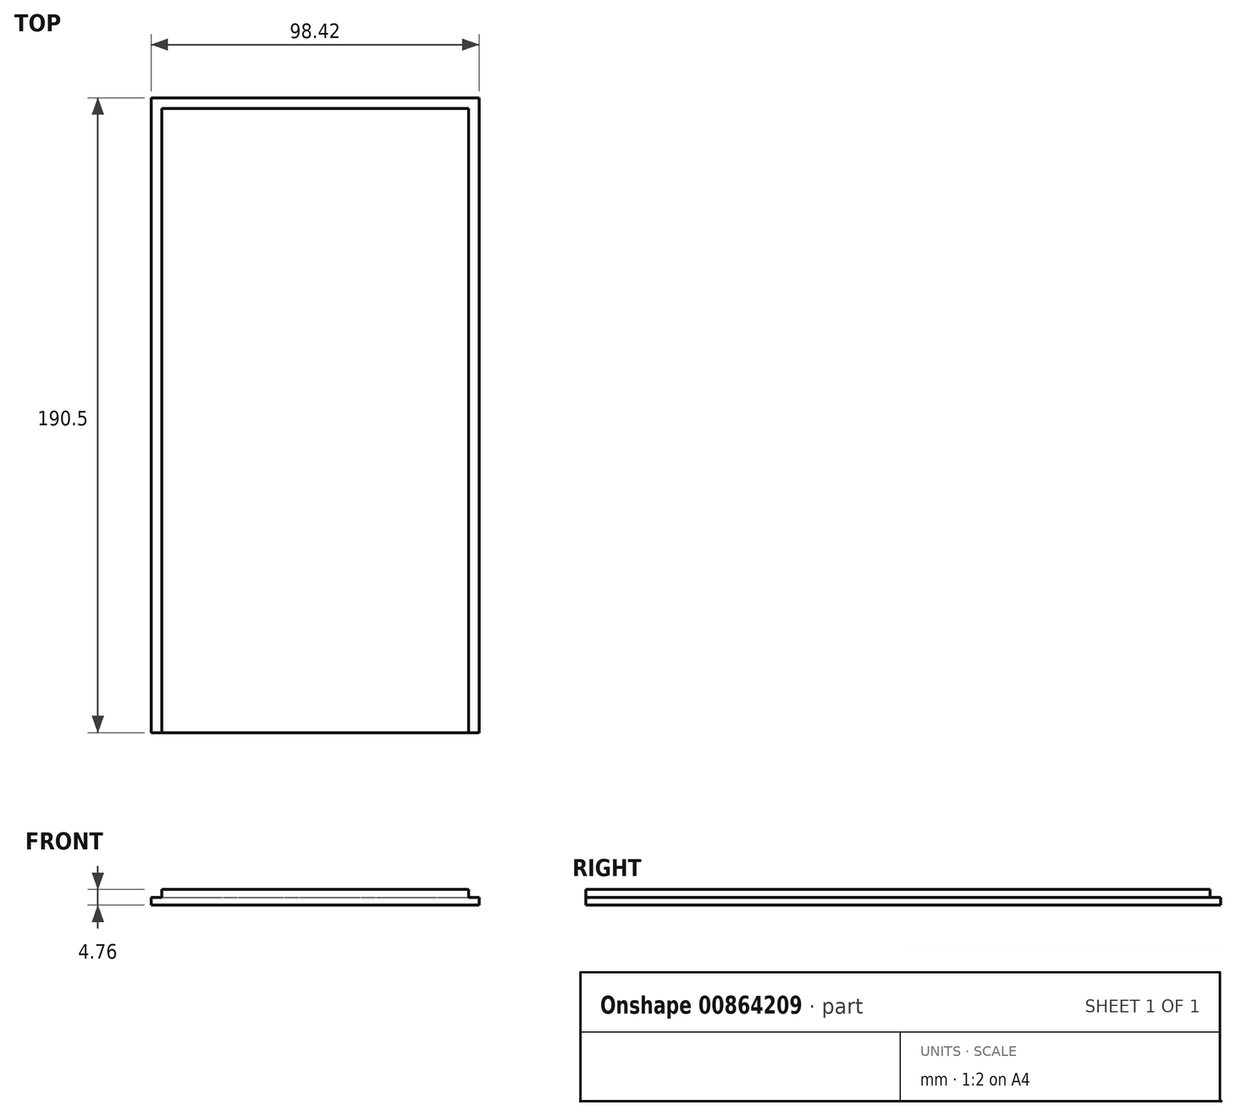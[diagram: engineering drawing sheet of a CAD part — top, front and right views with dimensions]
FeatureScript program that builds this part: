
annotation { "Feature Type Name" : "Feature", "Feature Type Description" : "" }
export const myFeature = defineFeature(function(context is Context, id is Id, definition is map)
    precondition{}
    {
        {
            var Q0;
            Q0=qCreatedBy(makeId("Top.planeOp"),FACE);
            var sketch = newSketch(context, id + "F0", { "sketchPlane" : qUnion([Q0])});
            skLineSegment(sketch, "E0.bottom", {"start": v(-49.21, 95.25) * mm, "end": v(49.21, 95.25) * mm});
            skLineSegment(sketch, "E0.top", {"start": v(-49.21, -95.25) * mm, "end": v(49.21, -95.25) * mm});
            skLineSegment(sketch, "E0.left", {"start": v(-49.21, 95.25) * mm, "end": v(-49.21, -95.25) * mm});
            skLineSegment(sketch, "E0.right", {"start": v(49.21, 95.25) * mm, "end": v(49.21, -95.25) * mm});
            skPoint(sketch, "E0.middle", {"position": v(0, 0) * mm});
            skLineSegment(sketch, "E1", {"start": v(-46.04, -95.25) * mm, "end": v(-46.04, 92.08) * mm});
            skLineSegment(sketch, "E2", {"start": v(-46.04, 92.08) * mm, "end": v(46.04, 92.08) * mm});
            skLineSegment(sketch, "E3", {"start": v(46.04, 92.08) * mm, "end": v(46.04, -95.25) * mm});
            skSolve(sketch);
        }
        {
            var Q0;
            {var subQ0=sQuery(id+"F0.wireOp",EDGE,"E1");Q0=makeQuery(id+"F0.imprint","IMPRINT",FACE,{"disambiguationData":[TD([[makeQuery(id+"F0.imprint","IMPRINT",EDGE,{"derivedFrom":subQ0}),-1.0]])]});}
            extrude(context, id + "F1", {"entities" : qUnion([Q0]), "depth" : 4.76 * mm, "offsetDistance" : 25.4 * mm});
        }
        {
            var Q0;
            Q0=makeQuery(id+"F0.imprint","IMPRINT",FACE,{"disambiguationData":[TD([[makeQuery(id+"F0.imprint","IMPRINT",EDGE,{"derivedFrom":sQuery(id+"F0.wireOp",EDGE,"E0.bottom")}),-1.0]])]});
            extrude(context, id + "F2", {"entities" : qUnion([Q0]), "operationType" : NewBodyOperationType.ADD, "depth" : 2.4 * mm, "offsetDistance" : 25.4 * mm});
        }
    });
